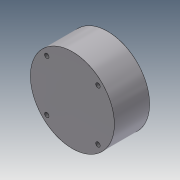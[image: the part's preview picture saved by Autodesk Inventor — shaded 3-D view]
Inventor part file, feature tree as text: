
AUTODESK INVENTOR PART (.ipt)
format: ipt  version: 2018.3 (Build 223284000, 284)  size: 114,688 bytes
history: native  units: in
note: dims shown in document units (in); Inventor stores cm internally (conversion verified against a paired STEP export)
features: sketch x3, hole x2, extrude x1, pattern_circular x1
ambient origin geometry x8: Origin, YZ Plane, XZ Plane, XY Plane, X Axis, Y Axis, Z Axis, Center Point
bodies: Solid1 (feature_tree)
feature tree (7):
  extrude  "Extrusion1"  Depth=3.12in
  hole  "Hole1"  [1 undecoded]
  hole  "Hole2"  [1 undecoded]
  pattern_circular  "Circular Pattern1"  [2 undecoded]
  sketch  "Sketch1"  dims[d0=0.8125in d1=3.12in]
  sketch  "Sketch2"  dims[d2=1.06in d3=0.0in]
  sketch  "Sketch3"  dims[d5=0.163in d6=0.394in d7=0.375in d8=0.25in d9=0.5635in d10=0.559in d11=0.8108in d12=1.5748in d13=360.0deg d15=0.163in d16=0.394in d17=0.375in d18=0.25in d19=0.5635in d20=0.559in d21=0.8108in d22=1.902in]
note: 4 required parameter values undecoded (feature->parameter linkage not recoverable at this tier; creation-order binding heuristic only, values carry confidence <= 0.55)
